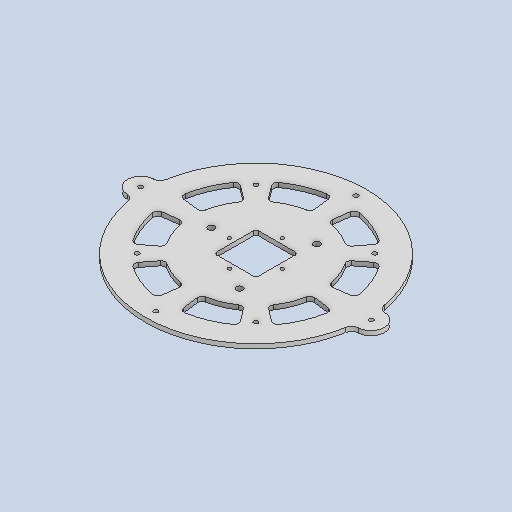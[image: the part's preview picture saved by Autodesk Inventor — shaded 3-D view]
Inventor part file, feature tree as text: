
AUTODESK INVENTOR PART (.ipt)
format: ipt  version: 2025.1 (Build 291241020, 241B)  size: 921,088 bytes
history: native  units: in
note: dims shown in document units (in); Inventor stores cm internally (conversion verified against a paired STEP export)
features: sketch x8, extrude x5, split x3, fillet x2
ambient origin geometry x8: Origin, YZ Plane, XZ Plane, XY Plane, X Axis, Y Axis, Z Axis, Center Point
bodies: Solid35 (feature_tree), Solid40 (feature_tree), Solid41 (feature_tree)
feature tree (18):
  extrude  "Extrusion1"  Depth=2.3661in
  fillet  "Fillet1"  Radius=2.3661in
  extrude  "Extrusion3"  Depth=2.3661in
  extrude  "Extrusion2"  Depth=0.1575in
  fillet  "Fillet5"  Radius=0.201in
  sketch  "Sketch5"  dims[d10=0.201in d11=2.9921in]
  split  "Split17"
  split  "Split18"
  split  "Split19"
  sketch  "Sketch8"  dims[d13=2.9921in]
  sketch  "Sketch9"  dims[d14=1.4961in d15=0.375in d17=4.358in d20=0.375in d24=0.2525in d25=0.2525in d26=11.311in d27=5.6555in d30=1.5in d31=0.2525in d33=13.01in d34=0.25in d35=0.0in d36=0.4in d38=4.358in d39=4.358in d41=5.0322in d54=0.25in d55=0.0in d79=0.25in d80=0.25in d81=0.25in d82=0.25in d83=9.5in d84=6.7175in d85=6.7175in d86=9.5in d87=0.25in d88=0.0in d94=3.3588in d95=3.3588in d96=10.0in d97=7.25in d98=15.0deg d99=0.2577in d100=3.1496in d102=360.0deg d104=0.25in d107=0.125in d108=0.125in d109=0.125in d119=0.4573in d120=0.4162in d121=0.3519in d122=0.6651in d123=0.379in d124=0.2188in d125=0.383in d126=0.735in d127=0.5332in d128=0.2522in d129=0.3287in d130=0.0218in d131=0.125in d132=0.3485in d133=0.0777in d135=1.0in d136=1.0in d137=1.0in d138=1.0in d139=1.0in d140=1.0in d141=1.0in d142=1.0in d143=0.0in d144=0.0in d145=0.0in d146=0.0in d147=1.0in d148=1.0in d149=1.0in d150=1.0in]
  extrude  "Extrusion4"  Depth=0.201in
  extrude  "Extrusion5"  Depth=2.9921in
  sketch  "Sketch1"  dims[d0=12.5in d1=1.1831in d2=2.3661in]
  sketch  "Sketch2"  dims[d3=2.3661in d4=1.1831in]
  sketch  "Sketch4"  dims[d5=0.1575in d6=0.1575in d7=0.201in]
  sketch  "Sketch Circular Pattern4"  dims[d8=0.201in d9=0.201in]
  sketch  "Sketch6"  dims[d12=1.4961in]
